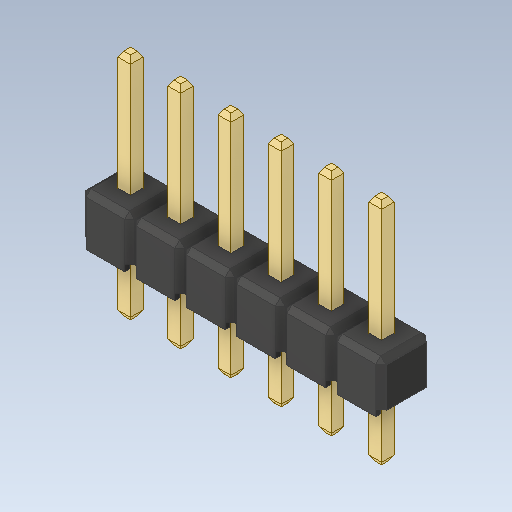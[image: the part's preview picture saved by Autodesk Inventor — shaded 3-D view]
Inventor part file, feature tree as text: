
AUTODESK INVENTOR PART (.ipt)
format: ipt  version: 2020 (Build 240168000, 168)  size: 275,968 bytes
history: native  units: in
note: dims shown in document units (in); Inventor stores cm internally (conversion verified against a paired STEP export)
features: other x11, chamfer x1
ambient origin geometry x8: Origin, YZ Plane, XZ Plane, XY Plane, X Axis, Y Axis, Z Axis, Center Point
bodies: Solid1 (feature_tree), Solid2 (feature_tree), Solid3 (feature_tree), Solid4 (feature_tree), Solid5 (feature_tree), Solid6 (feature_tree), Solid7 (feature_tree), Solid8 (feature_tree), Solid9 (feature_tree), Solid10 (feature_tree), Solid11 (feature_tree), Solid12 (feature_tree)
feature tree (12):
  chamfer  "Chamfer2"  [1 undecoded]
  other  "Boss-Extrude3"
  other  "LPattern1[1]"
  other  "LPattern1[2]"
  other  "LPattern1[3]"
  other  "LPattern1[4]"
  other  "LPattern1[5]"
  other  "LPattern1[6]"
  other  "LPattern1[7]"
  other  "LPattern1[8]"
  other  "LPattern1[9]"
  other  "LPattern1[10]"
note: 1 required parameter value undecoded (feature->parameter linkage not recoverable at this tier; creation-order binding heuristic only, values carry confidence <= 0.55)
